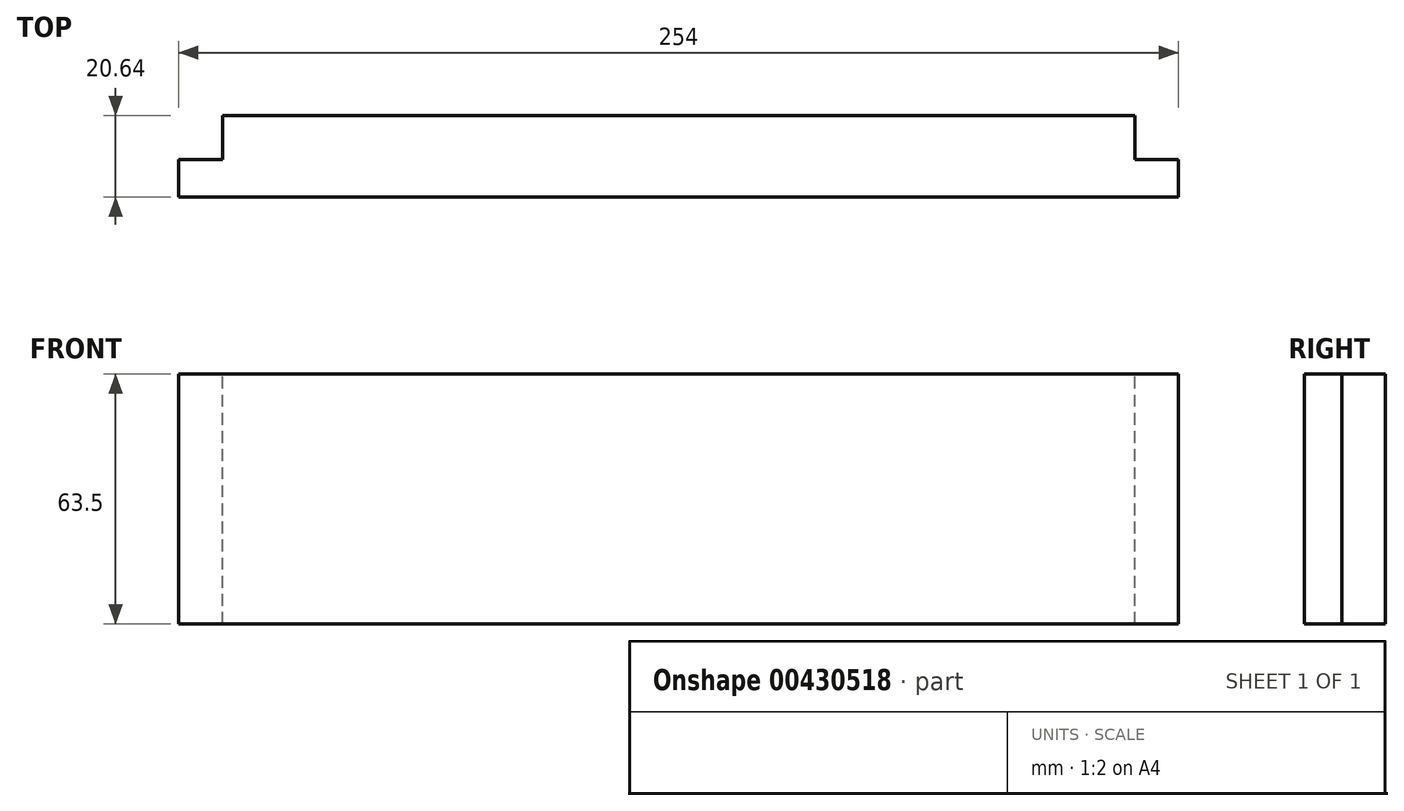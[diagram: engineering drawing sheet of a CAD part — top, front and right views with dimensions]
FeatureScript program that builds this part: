
annotation { "Feature Type Name" : "Feature", "Feature Type Description" : "" }
export const myFeature = defineFeature(function(context is Context, id is Id, definition is map)
    precondition{}
    {
        {
            var Q0;
            Q0=qCreatedBy(makeId("Top.planeOp"),FACE);
            var sketch = newSketch(context, id + "F0", { "sketchPlane" : qUnion([Q0])});
            skLineSegment(sketch, "E0", {"start": v(-127, 0) * mm, "end": v(127, 0) * mm});
            skLineSegment(sketch, "E1", {"start": v(127, 0) * mm, "end": v(127, 20.64) * mm});
            skLineSegment(sketch, "E2", {"start": v(127, 20.64) * mm, "end": v(-127, 20.64) * mm});
            skLineSegment(sketch, "E3", {"start": v(-127, 20.64) * mm, "end": v(-127, 0) * mm});
            skSolve(sketch);
        }
        {
            var Q0;
            Q0=makeQuery(id+"F0.imprint","IMPRINT",FACE,{"disambiguationData":[TD([[makeQuery(id+"F0.imprint","IMPRINT",EDGE,{"derivedFrom":sQuery(id+"F0.wireOp",EDGE,"E0")}),1.0]])]});
            extrude(context, id + "F1", {"entities" : qUnion([Q0]), "oppositeDirection" : true, "depth" : 63.5 * mm});
        }
        {
            var Q0;
            Q0=makeQuery(id+"F1.opExtrude","CAP_FACE",FACE,{"disambiguationData":[OSD([sQuery(id+"F0.wireOp",EDGE,"E0"),sQuery(id+"F0.wireOp",EDGE,"E1"),sQuery(id+"F0.wireOp",EDGE,"E2"),sQuery(id+"F0.wireOp",EDGE,"E3")])],"isStart":true});
            var sketch = newSketch(context, id + "F2", { "sketchPlane" : qUnion([Q0])});
            skLineSegment(sketch, "E4.bottom", {"start": v(-127, 20.64) * mm, "end": v(-115.89, 20.64) * mm});
            skLineSegment(sketch, "E4.top", {"start": v(-127, 9.53) * mm, "end": v(-115.89, 9.53) * mm});
            skLineSegment(sketch, "E4.left", {"start": v(-127, 20.64) * mm, "end": v(-127, 9.53) * mm});
            skLineSegment(sketch, "E4.right", {"start": v(-115.89, 20.64) * mm, "end": v(-115.89, 9.53) * mm});
            skLineSegment(sketch, "E5.bottom", {"start": v(127, 20.64) * mm, "end": v(115.89, 20.64) * mm});
            skLineSegment(sketch, "E5.top", {"start": v(127, 9.52) * mm, "end": v(115.89, 9.52) * mm});
            skLineSegment(sketch, "E5.left", {"start": v(127, 20.64) * mm, "end": v(127, 9.52) * mm});
            skLineSegment(sketch, "E5.right", {"start": v(115.89, 20.64) * mm, "end": v(115.89, 9.52) * mm});
            skSolve(sketch);
        }
        {
            var Q0;
            Q0 = qSketchRegion(id + "F2", true);
            extrude(context, id + "F3", {"entities" : qUnion([Q0]), "operationType" : NewBodyOperationType.REMOVE, "endBound" : BoundingType.THROUGH_ALL, "oppositeDirection" : true, "depth" : 25.4 * mm, "offsetDistance" : 25.4 * mm});
        }
    });
